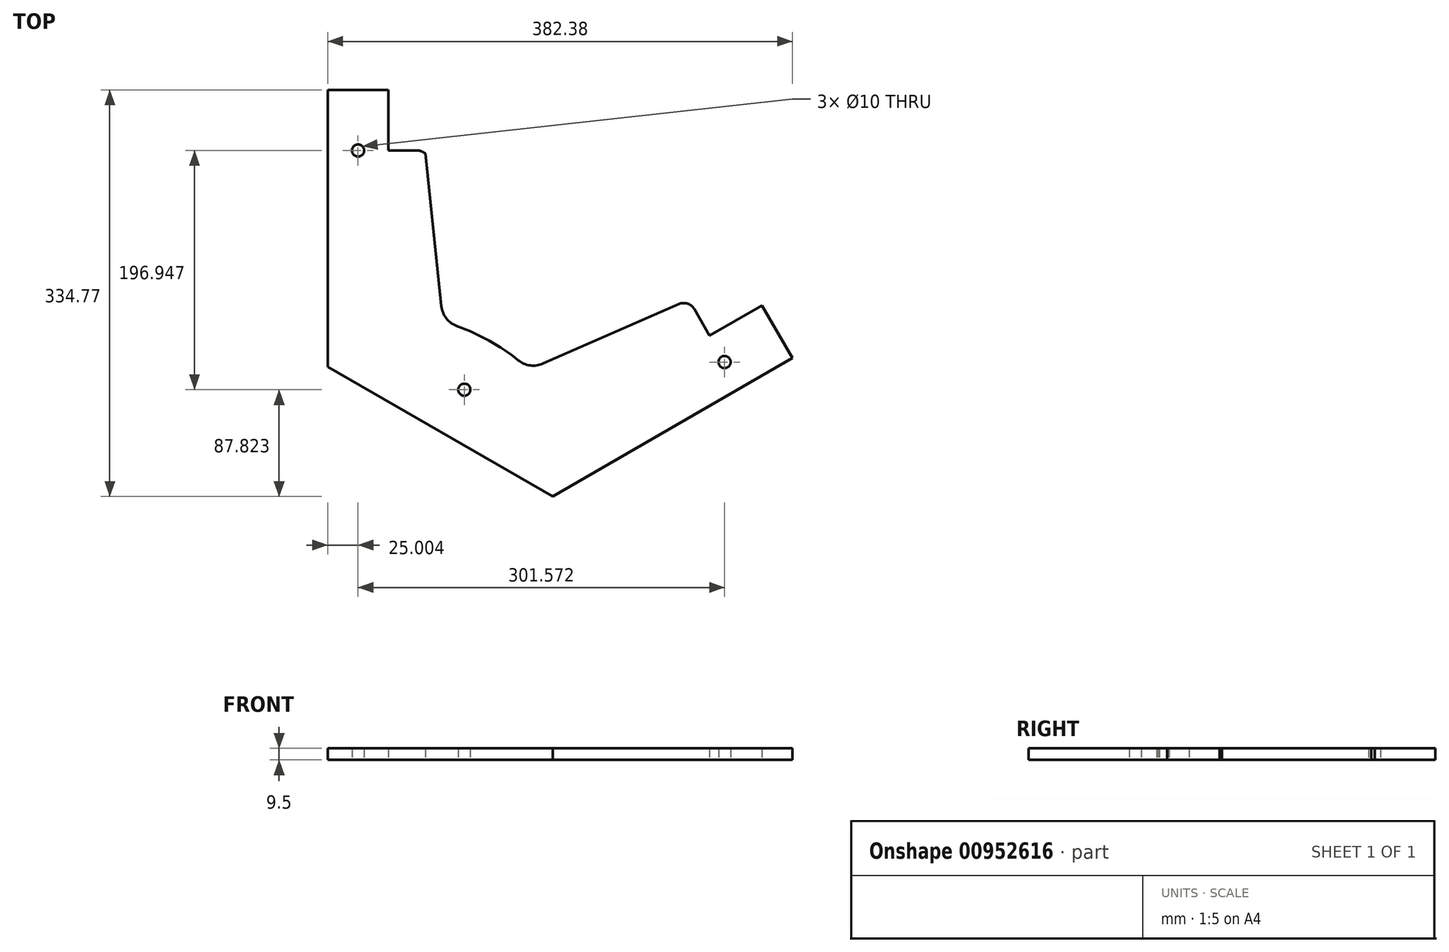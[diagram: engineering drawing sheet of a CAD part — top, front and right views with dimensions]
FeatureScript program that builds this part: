
annotation { "Feature Type Name" : "Feature", "Feature Type Description" : "" }
export const myFeature = defineFeature(function(context is Context, id is Id, definition is map)
    precondition{}
    {
        {
            var Q0;
            Q0=qCreatedBy(makeId("Top.planeOp"),FACE);
            var sketch = newSketch(context, id + "F0", { "sketchPlane" : qUnion([Q0])});
            skLineSegment(sketch, "E0", {"start": v(238.8, 178.56) * mm, "end": v(139.46, 134.92) * mm});
            skPoint(sketch, "E1.visualSharp", {"position": v(34.48, 45614.1) * mm});
            skLineSegment(sketch, "E2", {"start": v(23.54, 305) * mm, "end": v(-0.07, 305) * mm});
            skPoint(sketch, "E3.visualSharp", {"position": v(34.13, 305) * mm});
            skArc(sketch, "E3.filletArc", {"start": v(30.27, 302.4) * mm, "mid": v(27.15, 304.33) * mm, "end": v(23.54, 305) * mm});
            skPoint(sketch, "E4.visualSharp", {"position": v(247, 182.17) * mm});
            skArc(sketch, "E4.filletArc", {"start": v(247, 182.16) * mm, "mid": v(246.97, 182.15) * mm, "end": v(246.94, 182.14) * mm});
            skLineSegment(sketch, "E5", {"start": v(-0.07, 305) * mm, "end": v(-0.07, 355) * mm});
            skLineSegment(sketch, "E6", {"start": v(-0.07, 355) * mm, "end": v(-50.07, 355) * mm});
            skLineSegment(sketch, "E7", {"start": v(307.3, 177.5) * mm, "end": v(332.3, 134.2) * mm});
            skLineSegment(sketch, "E8", {"start": v(-50.07, 355) * mm, "end": v(-50.07, 127.01) * mm});
            skLineSegment(sketch, "E9", {"start": v(332.3, 134.2) * mm, "end": v(135, 20.23) * mm});
            skLineSegment(sketch, "E10", {"start": v(-50.07, 127.01) * mm, "end": v(135, 20.23) * mm});
            skCircle(sketch, "E11", {"center": v(276.5, 130.84) * mm, "radius": 5 * mm});
            skCircle(sketch, "E12", {"center": v(-25.07, 305) * mm, "radius": 5 * mm});
            skCircle(sketch, "E13", {"center": v(62.33, 108.05) * mm, "radius": 5 * mm});
            skLineSegment(sketch, "E14", {"start": v(62.33, 108.05) * mm, "end": v(59.83, 103.72) * mm});
            skPoint(sketch, "E15.orphan", {"position": v(42.46, 73.62) * mm});
            skLineSegment(sketch, "E16", {"start": v(139.46, 134.92) * mm, "end": v(127.31, 129.58) * mm});
            skLineSegment(sketch, "E17", {"start": v(30.27, 302.4) * mm, "end": v(43.43, 177.02) * mm});
            skPoint(sketch, "E18.visualSharp", {"position": v(44.79, 164.11) * mm});
            skArc(sketch, "E18.filletArc", {"start": v(43.43, 177.02) * mm, "mid": v(47.62, 166.72) * mm, "end": v(56.66, 160.25) * mm});
            skArc(sketch, "E19.trimOffspring", {"start": v(106.72, 132.32) * mm, "mid": v(82.87, 148.41) * mm, "end": v(56.66, 160.25) * mm});
            skPoint(sketch, "E20.visualSharp", {"position": v(115.75, 124.5) * mm});
            skArc(sketch, "E20.filletArc", {"start": v(106.72, 132.32) * mm, "mid": v(116.63, 128.07) * mm, "end": v(127.31, 129.58) * mm});
            skPoint(sketch, "E21.start.orphan", {"position": v(259.64, 160.03) * mm});
            skLineSegment(sketch, "E22", {"start": v(251.48, 174.4) * mm, "end": v(264.1, 152.55) * mm});
            skLineSegment(sketch, "E23.trimOffspring", {"start": v(-0.06, 305) * mm, "end": v(-0.07, 355) * mm});
            skLineSegment(sketch, "E24.trimOffspring", {"start": v(264.1, 152.55) * mm, "end": v(307.3, 177.5) * mm});
            skPoint(sketch, "E25.start.orphan", {"position": v(0, 0) * mm});
            skArc(sketch, "E26.filletArc", {"start": v(251.48, 174.4) * mm, "mid": v(245.94, 178.9) * mm, "end": v(238.8, 178.56) * mm});
            skSolve(sketch);
        }
        {
            var Q0;
            Q0 = qSketchRegion(id + "F0", true);
            extrude(context, id + "F1", {"entities" : qUnion([Q0]), "depth" : 9.5 * mm, "offsetDistance" : 25 * mm});
        }
    });
